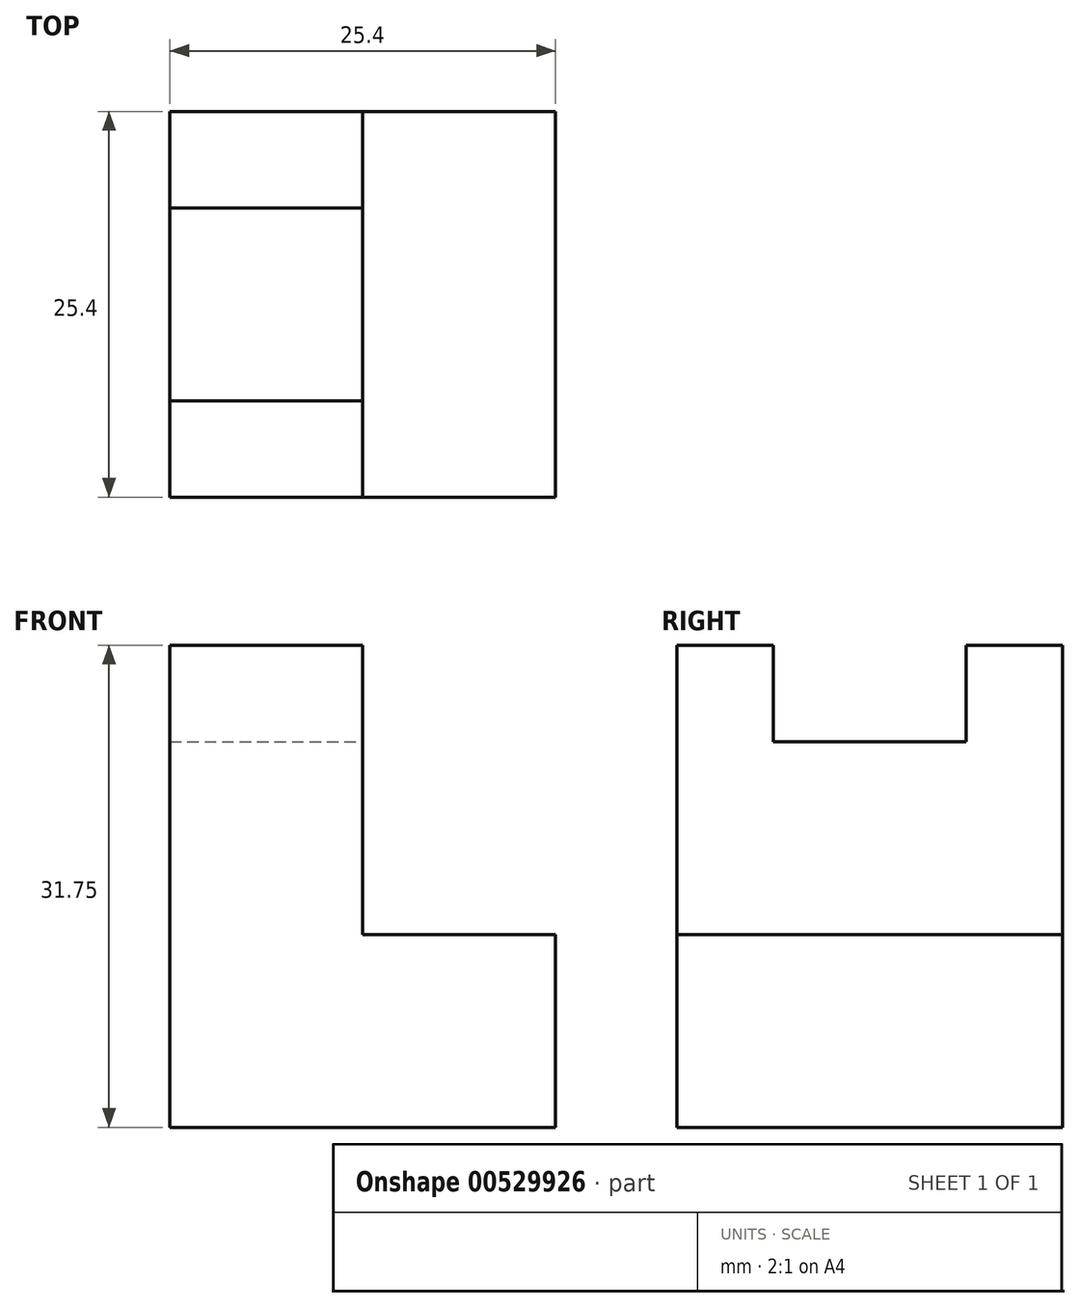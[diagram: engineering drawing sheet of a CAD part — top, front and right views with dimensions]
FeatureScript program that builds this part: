
annotation { "Feature Type Name" : "Feature", "Feature Type Description" : "" }
export const myFeature = defineFeature(function(context is Context, id is Id, definition is map)
    precondition{}
    {
        {
            var Q0;
            Q0=qCreatedBy(makeId("Front.planeOp"),FACE);
            var sketch = newSketch(context, id + "F0", { "sketchPlane" : qUnion([Q0])});
            skLineSegment(sketch, "E0", {"start": v(-59.34, 42.04) * mm, "end": v(-59.34, 10.3) * mm});
            skLineSegment(sketch, "E1", {"start": v(-59.34, 10.3) * mm, "end": v(-33.94, 10.3) * mm});
            skLineSegment(sketch, "E2", {"start": v(-33.94, 10.3) * mm, "end": v(-33.94, 23) * mm});
            skLineSegment(sketch, "E3", {"start": v(-33.94, 23) * mm, "end": v(-46.64, 23) * mm});
            skLineSegment(sketch, "E4", {"start": v(-46.64, 23) * mm, "end": v(-46.64, 42.04) * mm});
            skLineSegment(sketch, "E5", {"start": v(-46.64, 42.04) * mm, "end": v(-59.34, 42.04) * mm});
            skSolve(sketch);
        }
        {
            var Q0;
            Q0=makeQuery(id+"F0.imprint","IMPRINT",FACE,{"disambiguationData":[TD([[makeQuery(id+"F0.imprint","IMPRINT",EDGE,{"derivedFrom":sQuery(id+"F0.wireOp",EDGE,"E0")}),1.0]])]});
            extrude(context, id + "F1", {"entities" : qUnion([Q0]), "depth" : 25.4 * mm, "offsetDistance" : 25.4 * mm});
        }
        {
            var Q0;
            Q0=makeQuery(id+"F1.opExtrude","SWEPT_FACE",FACE,{"disambiguationData":[OSD([sQuery(id+"F0.wireOp",EDGE,"E4")])]});
            var sketch = newSketch(context, id + "F2", { "sketchPlane" : qUnion([Q0])});
            skLineSegment(sketch, "E6", {"start": v(-19.05, 42.04) * mm, "end": v(-19.05, 35.7) * mm});
            skLineSegment(sketch, "E7", {"start": v(-19.05, 35.7) * mm, "end": v(-6.35, 35.7) * mm});
            skLineSegment(sketch, "E8", {"start": v(-6.35, 35.7) * mm, "end": v(-6.35, 42.04) * mm});
            skSolve(sketch);
        }
        {
            var Q0;
            {var subQ0=sQuery(id+"F2.wireOp",EDGE,"E6");Q0=makeQuery(id+"F2.imprint","IMPRINT",FACE,{"disambiguationData":[TD([[makeQuery(id+"F2.imprint","IMPRINT",EDGE,{"derivedFrom":subQ0}),1.0]])]});}
            extrude(context, id + "F3", {"entities" : qUnion([Q0]), "operationType" : NewBodyOperationType.REMOVE, "oppositeDirection" : true, "depth" : 25.4 * mm, "offsetDistance" : 25.4 * mm});
        }
    });
